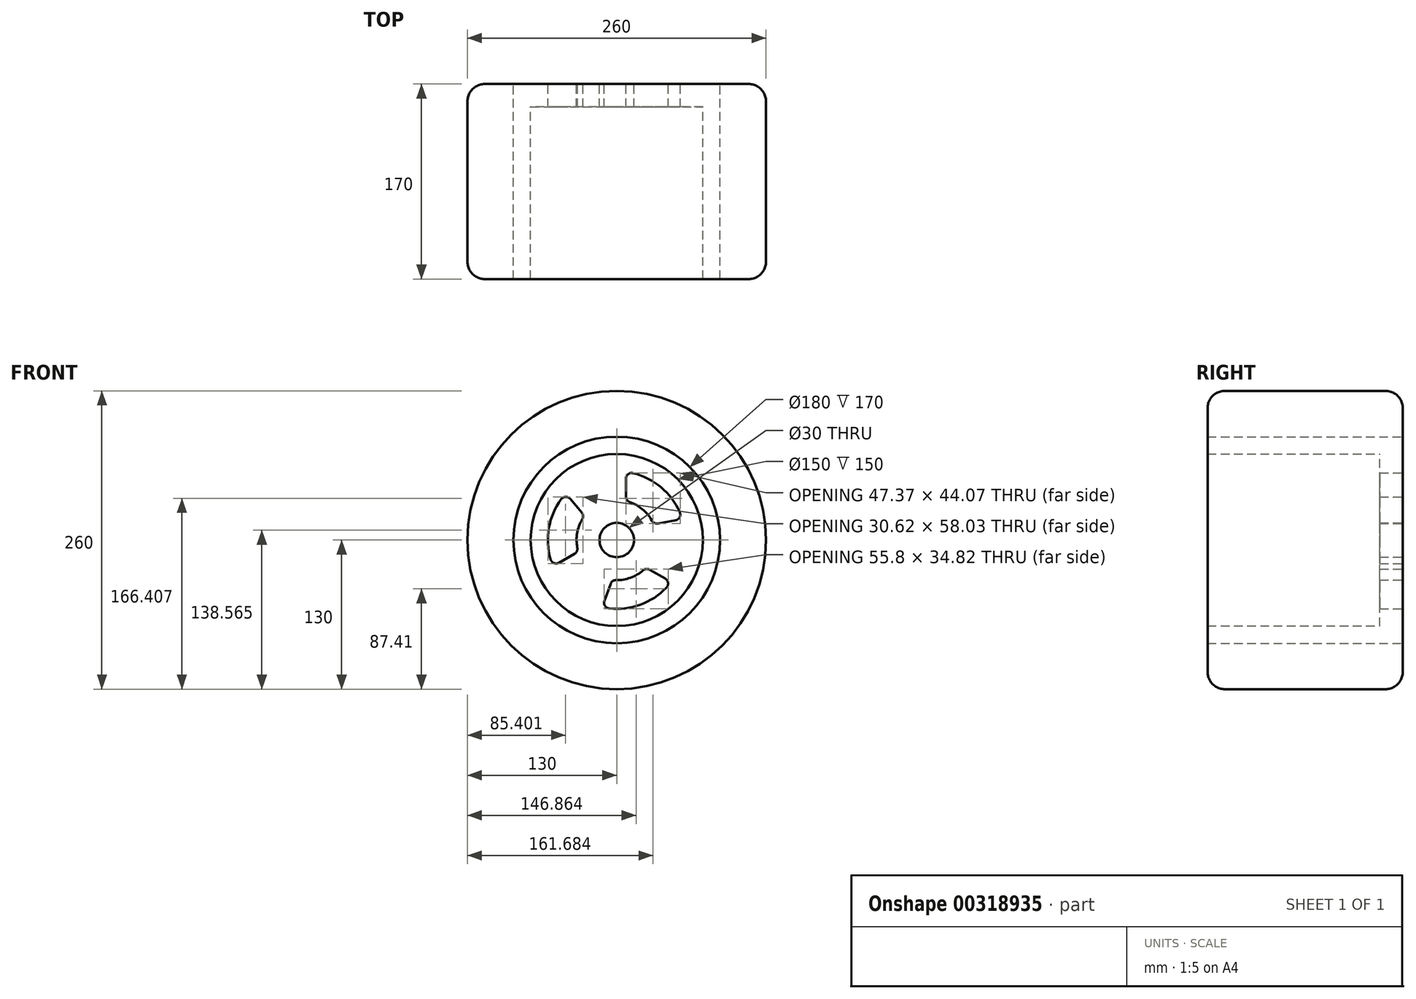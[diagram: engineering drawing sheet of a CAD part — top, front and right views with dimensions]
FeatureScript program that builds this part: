
annotation { "Feature Type Name" : "Feature", "Feature Type Description" : "" }
export const myFeature = defineFeature(function(context is Context, id is Id, definition is map)
    precondition{}
    {
        {
            var Q0;
            Q0=qCreatedBy(makeId("Front.planeOp"),FACE);
            var sketch = newSketch(context, id + "F0", { "sketchPlane" : qUnion([Q0])});
            skCircle(sketch, "E0", {"center": v(0, 0) * mm, "radius": 90 * mm});
            skCircle(sketch, "E1", {"center": v(0, 0) * mm, "radius": 15 * mm});
            skLineSegment(sketch, "E2", {"start": v(0, 0) * mm, "end": v(0, 85.59) * mm, "construction": true});
            skLineSegment(sketch, "E3", {"start": v(0, 0) * mm, "end": v(82.66, 14.58) * mm, "construction": true});
            skLineSegment(sketch, "E4", {"start": v(8, 53.44) * mm, "end": v(8, 37.83) * mm});
            skLineSegment(sketch, "E5", {"start": v(35.86, 14.45) * mm, "end": v(51.24, 17.16) * mm});
            skArc(sketch, "E6", {"start": v(54.95, 24.1) * mm, "mid": v(38.57, 45.96) * mm, "end": v(14.18, 58.3) * mm});
            skArc(sketch, "E7", {"start": v(30.62, 16.95) * mm, "mid": v(22.5, 26.81) * mm, "end": v(11.38, 33.1) * mm});
            skPoint(sketch, "E8.visualSharp", {"position": v(8, 59.46) * mm});
            skArc(sketch, "E8.filletArc", {"start": v(14.18, 58.3) * mm, "mid": v(9.91, 57.37) * mm, "end": v(8, 53.44) * mm});
            skPoint(sketch, "E9.visualSharp", {"position": v(57.17, 18.2) * mm});
            skArc(sketch, "E9.filletArc", {"start": v(51.24, 17.16) * mm, "mid": v(54.78, 19.72) * mm, "end": v(54.95, 24.1) * mm});
            skPoint(sketch, "E10.visualSharp", {"position": v(8, 34.07) * mm});
            skArc(sketch, "E10.filletArc", {"start": v(8, 37.83) * mm, "mid": v(8.93, 34.92) * mm, "end": v(11.38, 33.1) * mm});
            skPoint(sketch, "E11.visualSharp", {"position": v(32.17, 13.8) * mm});
            skArc(sketch, "E11.filletArc", {"start": v(30.62, 16.95) * mm, "mid": v(32.84, 14.86) * mm, "end": v(35.86, 14.45) * mm});
            skArc(sketch, "E12.1.0", {"start": v(-48.34, 35.54) * mm, "mid": v(-59.09, 10.42) * mm, "end": v(-57.58, -16.87) * mm});
            skArc(sketch, "E12.1.1", {"start": v(-40.48, 35.8) * mm, "mid": v(-44.47, 37.58) * mm, "end": v(-48.34, 35.54) * mm});
            skLineSegment(sketch, "E12.1.2", {"start": v(-30.44, 23.84) * mm, "end": v(-40.48, 35.8) * mm});
            skArc(sketch, "E12.1.3", {"start": v(-30, 18.04) * mm, "mid": v(-34.47, 6.08) * mm, "end": v(-34.35, -6.7) * mm});
            skLineSegment(sketch, "E12.1.4", {"start": v(-50.28, -19.8) * mm, "end": v(-36.76, -11.99) * mm});
            skArc(sketch, "E12.1.5", {"start": v(-57.58, -16.87) * mm, "mid": v(-54.64, -20.1) * mm, "end": v(-50.28, -19.8) * mm});
            skArc(sketch, "E12.1.6", {"start": v(-36.76, -11.99) * mm, "mid": v(-34.71, -9.73) * mm, "end": v(-34.35, -6.7) * mm});
            skArc(sketch, "E12.1.7", {"start": v(-30, 18.04) * mm, "mid": v(-29.29, 21.01) * mm, "end": v(-30.44, 23.84) * mm});
            skArc(sketch, "E12.2.0", {"start": v(-6.61, -59.63) * mm, "mid": v(20.52, -56.38) * mm, "end": v(43.4, -41.43) * mm});
            skArc(sketch, "E12.2.1", {"start": v(-10.76, -52.95) * mm, "mid": v(-10.3, -57.3) * mm, "end": v(-6.61, -59.63) * mm});
            skLineSegment(sketch, "E12.2.2", {"start": v(-5.42, -38.28) * mm, "end": v(-10.76, -52.95) * mm});
            skArc(sketch, "E12.2.3", {"start": v(-0.63, -35) * mm, "mid": v(11.97, -32.89) * mm, "end": v(22.98, -26.4) * mm});
            skLineSegment(sketch, "E12.2.4", {"start": v(42.28, -33.65) * mm, "end": v(28.76, -25.84) * mm});
            skArc(sketch, "E12.2.5", {"start": v(43.4, -41.43) * mm, "mid": v(44.73, -37.27) * mm, "end": v(42.28, -33.65) * mm});
            skArc(sketch, "E12.2.6", {"start": v(28.76, -25.84) * mm, "mid": v(25.78, -25.2) * mm, "end": v(22.98, -26.4) * mm});
            skArc(sketch, "E12.2.7", {"start": v(-0.63, -35) * mm, "mid": v(-3.55, -35.87) * mm, "end": v(-5.42, -38.28) * mm});
            skCircle(sketch, "E13", {"center": v(0, 0) * mm, "radius": 75 * mm});
            skSolve(sketch);
        }
        {
            var Q0;
            Q0=makeQuery(id+"F0.imprint","IMPRINT",FACE,{"disambiguationData":[TD([[makeQuery(id+"F0.imprint","IMPRINT",EDGE,{"derivedFrom":sQuery(id+"F0.wireOp",EDGE,"E1")}),-1.0]])]});
            extrude(context, id + "F1", {"entities" : qUnion([Q0]), "depth" : 20 * mm, "offsetDistance" : 25 * mm});
        }
        {
            var Q0;
            Q0 = qSketchRegion(id + "F0", true);
            extrude(context, id + "F2", {"entities" : qUnion([Q0]), "operationType" : NewBodyOperationType.ADD, "depth" : 170 * mm, "offsetDistance" : 25 * mm});
        }
        {
            var Q0;
            Q0=makeQuery(id+"F1.opExtrude","CAP_FACE",FACE,{"disambiguationData":[OSD([sQuery(id+"F0.wireOp",EDGE,"E0"),sQuery(id+"F0.wireOp",EDGE,"E1")])],"isStart":true});
            var sketch = newSketch(context, id + "F3", { "sketchPlane" : qUnion([Q0])});
            skCircle(sketch, "E14", {"center": v(0, 0) * mm, "radius": 130 * mm});
            skSolve(sketch);
        }
        {
            var Q0;
            Q0=makeQuery(id+"F3.imprint","IMPRINT",FACE,{"disambiguationData":[TD([[makeQuery(id+"F3.imprint","IMPRINT",EDGE,{"derivedFrom":sQuery(id+"F3.wireOp",EDGE,"E14")}),1.0]])]});
            extrude(context, id + "F4", {"entities" : qUnion([Q0]), "oppositeDirection" : true, "depth" : 170 * mm, "offsetDistance" : 25 * mm});
        }
        {
            var Q0;
            Q0=makeQuery(id+"F4.opExtrude","CAP_EDGE",EDGE,{"disambiguationData":[OSD([sQuery(id+"F3.wireOp",EDGE,"E14")])],"isStart":false});
            var Q1;
            Q1=makeQuery(id+"F4.opExtrude","CAP_EDGE",EDGE,{"disambiguationData":[OSD([sQuery(id+"F3.wireOp",EDGE,"E14")])],"isStart":true});
            fillet(context, id + "F5", {"entities" : qUnion([Q0, Q1]), "radius" : 15 * mm, "tangentPropagation" : true, "allowEdgeOverflow" : false});
        }
    });
